# Revit family: qf_turbo_air_tcdd-36H-B_W-N
name_source: partatom
category: Specialty Equipment
revit_build: Autodesk Revit 2018 (Build: 20180423_1000(x64)
units: mm (PartAtom-declared; Revit-internal decimal feet)

## family parameters
Always vertical = Yes
Cut with Voids When Loaded = No
OmniClass Number = 23.40.40.11.17
OmniClass Title = Refrigerated Cases
Part Type = Normal
Room Calculation Point = No
Round Connector Dimension = Use Diameter
Shared = No
Work Plane-Based = No

## types (2) — shared parameters
Apparent Power = 805 VA
Assembly Code = E1090320
BTUH = 0.0 Btu/h
CE Approved = Yes
CSI MasterFormat = 11 41 13
Conn Plug = NEMA 5-15P
Cycle = 60 Hz
Depth = 2' - 6"
Description = Bakery/Deli Case, Open Air
Elec Conn Connection Height = 0' - 6"
FL Amps = 7 A
Foodservice Equipment Identifier = Yes
HP = 1/3
Height = 4' - 2 1/8"
LEED EA Credit = V4.1 EA credits are based on 50% GHG, 50% utility cost. See WATTS.
Length = 3' - 0 1/2"
Manufacturer = Turbo Air
Phase = 1
Plumbing Remarks = No drain is required.
Type Comments = Automatic condenser coil cleaning system standard
URL = www.turboairinc.com
URL Cutsheet = http://www.turboairinc.com
URL Recommended Spares List = http://www.turboairinc.com
Vent Material = QF_Stainless-Polished
Ventilation Remarks = Unit is designed to type I specifications and should not be placed near a vent or doorway.
Volts = 115 V
Weight in Pounds = 496
zero-valued in all types: Barcode

## per-type parameters (varying)
| type | Exterior Material | Model |
| TCDD-36H-B-N | QF_Plastic-Black-Fine Textured | TCDD-36H-B-N |
| TCDD36H-W-N | QF_Plastic-Opaque-White | TCDD-36H-W-N |

## geometry (parser evidence)
native form markers: Sweep x3
no freeform markers — native parametric forms only
